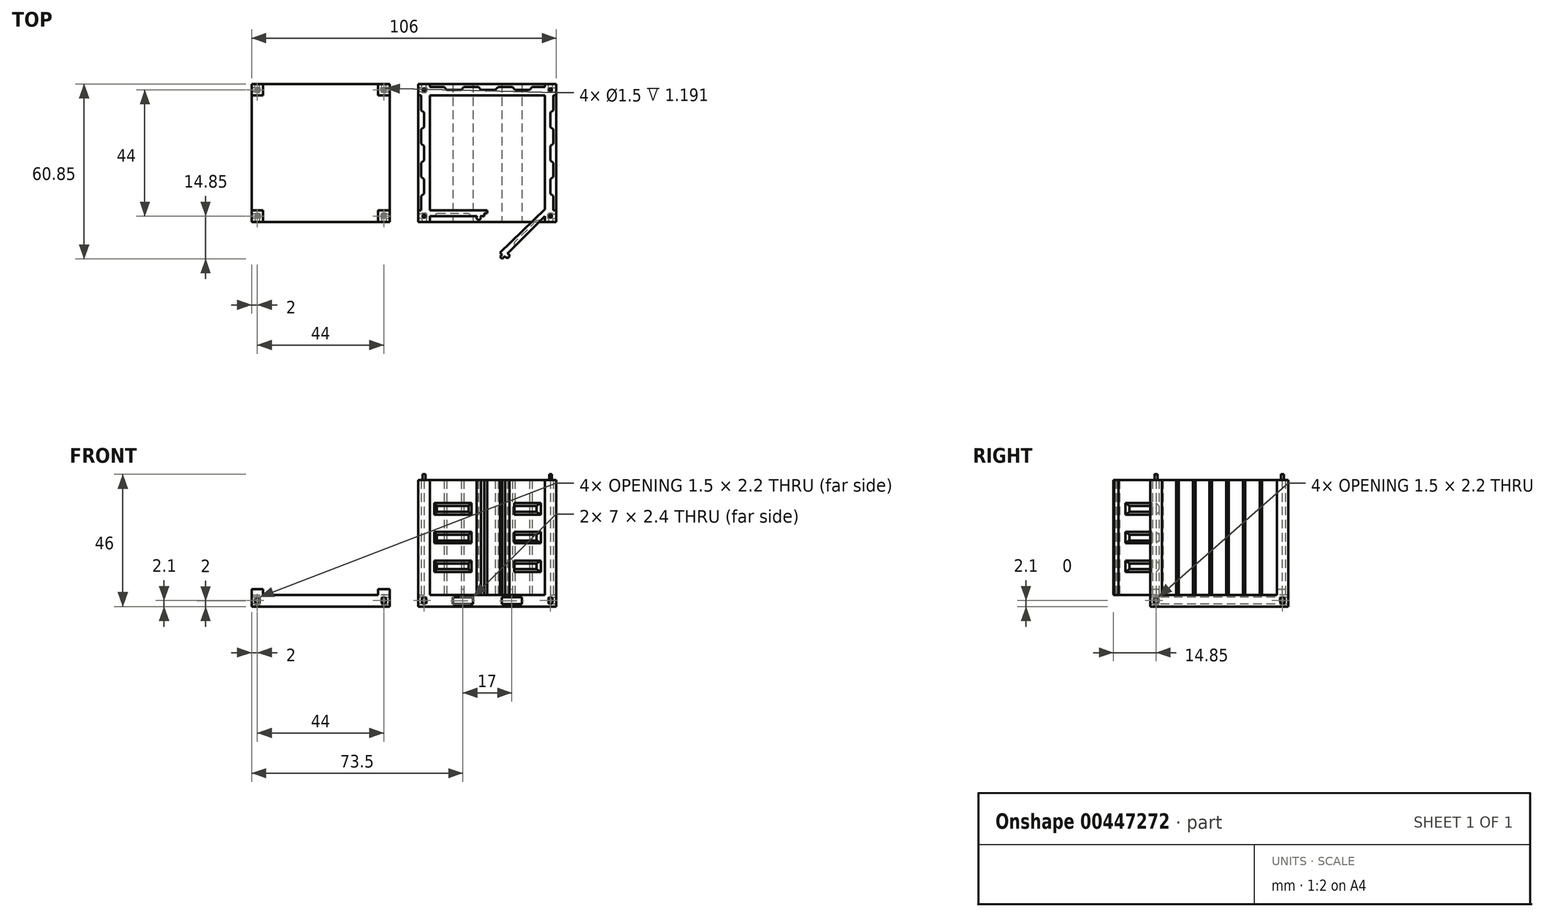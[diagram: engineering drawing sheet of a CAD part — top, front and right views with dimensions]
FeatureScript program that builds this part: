
annotation { "Feature Type Name" : "Feature", "Feature Type Description" : "" }
export const myFeature = defineFeature(function(context is Context, id is Id, definition is map)
    precondition{}
    {
        {
            var Q0;
            Q0=qCreatedBy(makeId("Top.planeOp"),FACE);
            var sketch = newSketch(context, id + "F0", { "sketchPlane" : qUnion([Q0])});
            skLineSegment(sketch, "E0.bottom", {"start": v(0, 0) * mm, "end": v(48, 0) * mm});
            skLineSegment(sketch, "E0.top", {"start": v(0, 48) * mm, "end": v(48, 48) * mm});
            skLineSegment(sketch, "E0.left", {"start": v(0, 0) * mm, "end": v(0, 48) * mm});
            skLineSegment(sketch, "E0.right", {"start": v(48, 0) * mm, "end": v(48, 48) * mm});
            skSolve(sketch);
        }
        {
            var Q0;
            Q0 = qSketchRegion(id + "F0", true);
            extrude(context, id + "F1", {"entities" : qUnion([Q0]), "depth" : 4 * mm});
        }
        {
            var Q0;
            Q0=makeQuery(id+"F1.opExtrude","SWEPT_FACE",FACE,{"disambiguationData":[OSD([sQuery(id+"F0.wireOp",EDGE,"E0.bottom")])]});
            var sketch = newSketch(context, id + "F2", { "sketchPlane" : qUnion([Q0])});
            skLineSegment(sketch, "E1", {"start": v(0, 2) * mm, "end": v(48, 2) * mm, "construction": true});
            skLineSegment(sketch, "E2", {"start": v(24, 2) * mm, "end": v(29, 2) * mm, "construction": true});
            skLineSegment(sketch, "E3", {"start": v(29, 2) * mm, "end": v(29, 3.2) * mm});
            skLineSegment(sketch, "E4", {"start": v(29, 3.2) * mm, "end": v(36, 3.2) * mm});
            skLineSegment(sketch, "E5", {"start": v(36, 3.2) * mm, "end": v(36, 0.8) * mm});
            skLineSegment(sketch, "E6", {"start": v(36, 0.8) * mm, "end": v(29, 0.8) * mm});
            skLineSegment(sketch, "E7", {"start": v(29, 0.8) * mm, "end": v(29, 2) * mm});
            skLineSegment(sketch, "E8", {"start": v(24, 2) * mm, "end": v(24, -4.17) * mm, "construction": true});
            skLineSegment(sketch, "E9.MirrorCS", {"start": v(19, 3.2) * mm, "end": v(12, 3.2) * mm});
            skLineSegment(sketch, "E10.MirrorCS", {"start": v(19, 2) * mm, "end": v(19, 3.2) * mm});
            skLineSegment(sketch, "E11.MirrorCS", {"start": v(19, 0.8) * mm, "end": v(19, 2) * mm});
            skLineSegment(sketch, "E12.MirrorCS", {"start": v(12, 0.8) * mm, "end": v(19, 0.8) * mm});
            skLineSegment(sketch, "E13.MirrorCS", {"start": v(12, 3.2) * mm, "end": v(12, 0.8) * mm});
            skSolve(sketch);
        }
        {
            var Q0;
            Q0 = qSketchRegion(id + "F2", true);
            extrude(context, id + "F3", {"entities" : qUnion([Q0]), "operationType" : NewBodyOperationType.REMOVE, "oppositeDirection" : true, "depth" : 48 * mm});
        }
        {
            var Q0;
            Q0=makeQuery(id+"F1.opExtrude","CAP_FACE",FACE,{"disambiguationData":[OSD([sQuery(id+"F0.wireOp",EDGE,"E0.bottom"),sQuery(id+"F0.wireOp",EDGE,"E0.top"),sQuery(id+"F0.wireOp",EDGE,"E0.left"),sQuery(id+"F0.wireOp",EDGE,"E0.right")])],"isStart":false});
            var sketch = newSketch(context, id + "F4", { "sketchPlane" : qUnion([Q0])});
            skLineSegment(sketch, "E14.bottom", {"start": v(0, 48) * mm, "end": v(4, 48) * mm});
            skLineSegment(sketch, "E14.top", {"start": v(0, 44) * mm, "end": v(1, 44) * mm});
            skLineSegment(sketch, "E14.left", {"start": v(0, 48) * mm, "end": v(0, 44) * mm});
            skLineSegment(sketch, "E14.right", {"start": v(4, 48) * mm, "end": v(4, 47) * mm});
            skLineSegment(sketch, "E15.bottom", {"start": v(48, 48) * mm, "end": v(44, 48) * mm});
            skLineSegment(sketch, "E15.top", {"start": v(48, 44) * mm, "end": v(47, 44) * mm});
            skLineSegment(sketch, "E15.left", {"start": v(48, 48) * mm, "end": v(48, 44) * mm});
            skLineSegment(sketch, "E15.right", {"start": v(44, 48) * mm, "end": v(44, 47) * mm});
            skLineSegment(sketch, "E16.bottom", {"start": v(48, 0) * mm, "end": v(44, 0) * mm});
            skLineSegment(sketch, "E16.top", {"start": v(48, 4) * mm, "end": v(47, 4) * mm});
            skLineSegment(sketch, "E16.left", {"start": v(48, 0) * mm, "end": v(48, 4) * mm});
            skLineSegment(sketch, "E16.right", {"start": v(44, 0) * mm, "end": v(44, 2) * mm});
            skLineSegment(sketch, "E17.bottom", {"start": v(0, 0) * mm, "end": v(4, 0) * mm});
            skLineSegment(sketch, "E17.top", {"start": v(0, 4) * mm, "end": v(1, 4) * mm});
            skLineSegment(sketch, "E17.left", {"start": v(0, 0) * mm, "end": v(0, 4) * mm});
            skLineSegment(sketch, "E17.right", {"start": v(4, 0) * mm, "end": v(4, 2) * mm});
            skLineSegment(sketch, "E18", {"start": v(1, 4) * mm, "end": v(0, 4) * mm, "construction": true});
            skLineSegment(sketch, "E19", {"start": v(1, 4) * mm, "end": v(1, 9) * mm});
            skLineSegment(sketch, "E20", {"start": v(1, 9) * mm, "end": v(2, 9.84) * mm});
            skLineSegment(sketch, "E21", {"start": v(2, 9.84) * mm, "end": v(2, 14.84) * mm});
            skLineSegment(sketch, "E22", {"start": v(2, 14.84) * mm, "end": v(1, 15.68) * mm});
            skLineSegment(sketch, "E23.0.1.0", {"start": v(1, 15.6) * mm, "end": v(1, 20.6) * mm});
            skLineSegment(sketch, "E23.0.1.1", {"start": v(1, 20.6) * mm, "end": v(2, 21.44) * mm});
            skLineSegment(sketch, "E23.0.1.2", {"start": v(2, 21.44) * mm, "end": v(2, 26.44) * mm});
            skLineSegment(sketch, "E23.0.1.3", {"start": v(2, 26.44) * mm, "end": v(1, 27.28) * mm});
            skLineSegment(sketch, "E23.0.2.0", {"start": v(1, 27.2) * mm, "end": v(1, 32.2) * mm});
            skLineSegment(sketch, "E23.0.2.1", {"start": v(1, 32.2) * mm, "end": v(2, 33.04) * mm});
            skLineSegment(sketch, "E23.0.2.2", {"start": v(2, 33.04) * mm, "end": v(2, 38.04) * mm});
            skLineSegment(sketch, "E23.0.2.3", {"start": v(2, 38.04) * mm, "end": v(1, 38.88) * mm});
            skLineSegment(sketch, "E23.direction1", {"start": v(1, 4) * mm, "end": v(1.1, 4.1) * mm, "construction": true});
            skLineSegment(sketch, "E23.direction2", {"start": v(1, 4) * mm, "end": v(1, 15.6) * mm, "construction": true});
            skLineSegment(sketch, "E24", {"start": v(1, 38.88) * mm, "end": v(1, 44) * mm});
            skLineSegment(sketch, "E25", {"start": v(24, 0) * mm, "end": v(24, -4.5) * mm, "construction": true});
            skLineSegment(sketch, "E26.MirrorCS", {"start": v(47, 9) * mm, "end": v(46, 9.84) * mm});
            skLineSegment(sketch, "E27.MirrorCS", {"start": v(46, 9.84) * mm, "end": v(46, 14.84) * mm});
            skLineSegment(sketch, "E28.MirrorCS", {"start": v(46, 14.84) * mm, "end": v(47, 15.68) * mm});
            skLineSegment(sketch, "E29.MirrorCS", {"start": v(47, 15.6) * mm, "end": v(47, 20.6) * mm});
            skLineSegment(sketch, "E30.MirrorCS", {"start": v(47, 20.6) * mm, "end": v(46, 21.44) * mm});
            skLineSegment(sketch, "E31.MirrorCS", {"start": v(46, 21.44) * mm, "end": v(46, 26.44) * mm});
            skLineSegment(sketch, "E32.MirrorCS", {"start": v(46, 26.44) * mm, "end": v(47, 27.28) * mm});
            skLineSegment(sketch, "E33.MirrorCS", {"start": v(47, 27.2) * mm, "end": v(47, 32.2) * mm});
            skLineSegment(sketch, "E34.MirrorCS", {"start": v(47, 32.2) * mm, "end": v(46, 33.04) * mm});
            skLineSegment(sketch, "E35.MirrorCS", {"start": v(46, 33.04) * mm, "end": v(46, 38.04) * mm});
            skLineSegment(sketch, "E36.MirrorCS", {"start": v(46, 38.04) * mm, "end": v(47, 38.88) * mm});
            skLineSegment(sketch, "E37.MirrorCS", {"start": v(47, 38.88) * mm, "end": v(47, 44) * mm});
            skLineSegment(sketch, "E38", {"start": v(47, 9) * mm, "end": v(47, 4) * mm});
            skLineSegment(sketch, "E39", {"start": v(4, 48) * mm, "end": v(4, 47) * mm, "construction": true});
            skLineSegment(sketch, "E40", {"start": v(4, 47) * mm, "end": v(9, 47) * mm});
            skLineSegment(sketch, "E41", {"start": v(9, 47) * mm, "end": v(9.93, 45.9) * mm});
            skLineSegment(sketch, "E42", {"start": v(9.93, 45.9) * mm, "end": v(14.93, 45.9) * mm});
            skLineSegment(sketch, "E43", {"start": v(14.93, 45.9) * mm, "end": v(15.86, 47) * mm});
            skLineSegment(sketch, "E44", {"start": v(15.86, 47) * mm, "end": v(20.86, 47) * mm});
            skLineSegment(sketch, "E45", {"start": v(20.86, 47) * mm, "end": v(21.79, 45.9) * mm});
            skLineSegment(sketch, "E46", {"start": v(21.79, 45.9) * mm, "end": v(26.79, 45.9) * mm});
            skLineSegment(sketch, "E47", {"start": v(26.79, 45.9) * mm, "end": v(27.71, 47) * mm});
            skLineSegment(sketch, "E48", {"start": v(27.71, 47) * mm, "end": v(32.71, 47) * mm});
            skLineSegment(sketch, "E49", {"start": v(32.71, 47) * mm, "end": v(33.64, 45.9) * mm});
            skLineSegment(sketch, "E50", {"start": v(33.64, 45.9) * mm, "end": v(38.64, 45.9) * mm});
            skLineSegment(sketch, "E51", {"start": v(38.64, 45.9) * mm, "end": v(39.57, 47) * mm});
            skLineSegment(sketch, "E52", {"start": v(39.57, 47) * mm, "end": v(44, 47) * mm});
            skLineSegment(sketch, "E53", {"start": v(4, 2) * mm, "end": v(20.44, 2) * mm});
            skLineSegment(sketch, "E54", {"start": v(23, 2) * mm, "end": v(23, 3) * mm});
            skLineSegment(sketch, "E55", {"start": v(23, 3) * mm, "end": v(24, 3) * mm});
            skLineSegment(sketch, "E56", {"start": v(24, 3) * mm, "end": v(24, 4) * mm});
            skLineSegment(sketch, "E57", {"start": v(24, 4) * mm, "end": v(4, 4) * mm});
            skLineSegment(sketch, "E58", {"start": v(44, 2) * mm, "end": v(30.96, -11.04) * mm});
            skLineSegment(sketch, "E59", {"start": v(29.15, -12.85) * mm, "end": v(28.44, -12.14) * mm});
            skLineSegment(sketch, "E60", {"start": v(28.44, -12.14) * mm, "end": v(29.15, -11.44) * mm});
            skLineSegment(sketch, "E61", {"start": v(29.15, -11.44) * mm, "end": v(28.44, -10.73) * mm});
            skLineSegment(sketch, "E62", {"start": v(28.44, -10.73) * mm, "end": v(44, 4.37) * mm});
            skLineSegment(sketch, "E63", {"start": v(44, 4.37) * mm, "end": v(44, 44) * mm});
            skLineSegment(sketch, "E64", {"start": v(44, 44) * mm, "end": v(4, 44) * mm});
            skLineSegment(sketch, "E65", {"start": v(4, 44) * mm, "end": v(4, 4) * mm});
            skPoint(sketch, "E66.orphan", {"position": v(4, 46) * mm});
            skPoint(sketch, "E67.orphan", {"position": v(44, 4) * mm});
            skPoint(sketch, "E68.orphan", {"position": v(2, 4) * mm});
            skLineSegment(sketch, "E69", {"start": v(23, 2) * mm, "end": v(21.56, 2) * mm, "construction": true});
            skLineSegment(sketch, "E70", {"start": v(21, 2) * mm, "end": v(21, 1.5) * mm, "construction": true});
            skArc(sketch, "E71", {"start": v(20.44, 2) * mm, "mid": v(21, 0.75) * mm, "end": v(21.56, 2) * mm});
            skLineSegment(sketch, "E72.trimOffspring", {"start": v(21.56, 2) * mm, "end": v(23, 2) * mm});
            skLineSegment(sketch, "E73", {"start": v(29.15, -12.85) * mm, "end": v(30.17, -11.83) * mm, "construction": true});
            skLineSegment(sketch, "E74", {"start": v(30.56, -11.44) * mm, "end": v(30.92, -11.79) * mm, "construction": true});
            skArc(sketch, "E75", {"start": v(30.17, -11.83) * mm, "mid": v(31.45, -12.32) * mm, "end": v(30.96, -11.04) * mm});
            skLineSegment(sketch, "E76.trimOffspring", {"start": v(30.17, -11.83) * mm, "end": v(29.15, -12.85) * mm});
            skSolve(sketch);
        }
        {
            var Q0;
            Q0 = qSketchRegion(id + "F4", true);
            extrude(context, id + "F5", {"entities" : qUnion([Q0]), "operationType" : NewBodyOperationType.ADD, "depth" : 40 * mm});
        }
        {
            var Q0;
            Q0=makeQuery(id+"F5.opExtrude","SWEPT_FACE",FACE,{"disambiguationData":[OSD([sQuery(id+"F4.wireOp",EDGE,"E53")])]});
            var sketch = newSketch(context, id + "F6", { "sketchPlane" : qUnion([Q0])});
            skLineSegment(sketch, "E77", {"start": v(4, 24) * mm, "end": v(5.5, 24) * mm, "construction": true});
            skLineSegment(sketch, "E78", {"start": v(5.5, 24) * mm, "end": v(5.5, 26) * mm});
            skLineSegment(sketch, "E79", {"start": v(5.5, 26) * mm, "end": v(18.5, 26) * mm});
            skLineSegment(sketch, "E80", {"start": v(18.5, 26) * mm, "end": v(18.5, 22) * mm});
            skLineSegment(sketch, "E81", {"start": v(18.5, 22) * mm, "end": v(5.5, 22) * mm});
            skLineSegment(sketch, "E82", {"start": v(5.5, 22) * mm, "end": v(5.5, 24) * mm});
            skLineSegment(sketch, "E83", {"start": v(4, 24) * mm, "end": v(4, 4) * mm, "construction": true});
            skPoint(sketch, "E84", {"position": v(4, 14) * mm});
            skLineSegment(sketch, "E85", {"start": v(4, 24) * mm, "end": v(4, 19) * mm, "construction": true});
            skLineSegment(sketch, "E86", {"start": v(4, 19) * mm, "end": v(-6.02, 19) * mm, "construction": true});
            skLineSegment(sketch, "E87.MirrorCS", {"start": v(5.5, 12) * mm, "end": v(18.5, 12) * mm});
            skLineSegment(sketch, "E88.MirrorCS", {"start": v(5.5, 14) * mm, "end": v(5.5, 12) * mm});
            skLineSegment(sketch, "E89.MirrorCS", {"start": v(5.5, 16) * mm, "end": v(5.5, 14) * mm});
            skLineSegment(sketch, "E90.MirrorCS", {"start": v(18.5, 16) * mm, "end": v(5.5, 16) * mm});
            skLineSegment(sketch, "E91.MirrorCS", {"start": v(18.5, 12) * mm, "end": v(18.5, 16) * mm});
            skLineSegment(sketch, "E92", {"start": v(4, 24) * mm, "end": v(4, 29) * mm, "construction": true});
            skLineSegment(sketch, "E93", {"start": v(4, 29) * mm, "end": v(-8.26, 29) * mm, "construction": true});
            skLineSegment(sketch, "E94.MirrorCS", {"start": v(5.5, 32) * mm, "end": v(18.5, 32) * mm});
            skLineSegment(sketch, "E95.MirrorCS", {"start": v(5.5, 34) * mm, "end": v(5.5, 32) * mm});
            skLineSegment(sketch, "E96.MirrorCS", {"start": v(5.5, 36) * mm, "end": v(5.5, 34) * mm});
            skLineSegment(sketch, "E97.MirrorCS", {"start": v(18.5, 36) * mm, "end": v(5.5, 36) * mm});
            skLineSegment(sketch, "E98.MirrorCS", {"start": v(18.5, 32) * mm, "end": v(18.5, 36) * mm});
            skSolve(sketch);
        }
        {
            var Q0;
            Q0 = qSketchRegion(id + "F6", true);
            extrude(context, id + "F7", {"entities" : qUnion([Q0]), "operationType" : NewBodyOperationType.REMOVE, "oppositeDirection" : true, "depth" : 1 * mm, "hasDraft" : true, "draftAngle" : 45 * degree, "draftPullDirection" : true});
        }
        {
            var Q0;
            Q0=makeQuery(id+"F5.opExtrude","SWEPT_FACE",FACE,{"disambiguationData":[OSD([sQuery(id+"F4.wireOp",EDGE,"E58")])]});
            var sketch = newSketch(context, id + "F8", { "sketchPlane" : qUnion([Q0])});
            skLineSegment(sketch, "E99", {"start": v(32.53, 24) * mm, "end": v(30.53, 24) * mm, "construction": true});
            skLineSegment(sketch, "E100", {"start": v(30.53, 24) * mm, "end": v(30.53, 22) * mm});
            skLineSegment(sketch, "E101", {"start": v(30.53, 22) * mm, "end": v(17.53, 22) * mm});
            skLineSegment(sketch, "E102", {"start": v(17.53, 22) * mm, "end": v(17.53, 26) * mm});
            skLineSegment(sketch, "E103", {"start": v(17.53, 26) * mm, "end": v(30.53, 26) * mm});
            skLineSegment(sketch, "E104", {"start": v(30.53, 26) * mm, "end": v(30.53, 24) * mm});
            skLineSegment(sketch, "E105", {"start": v(30.53, 24) * mm, "end": v(30.53, 29) * mm, "construction": true});
            skLineSegment(sketch, "E106", {"start": v(30.53, 29) * mm, "end": v(36.07, 29) * mm, "construction": true});
            skLineSegment(sketch, "E107.MirrorCS", {"start": v(17.53, 32) * mm, "end": v(30.53, 32) * mm});
            skLineSegment(sketch, "E108.MirrorCS", {"start": v(17.53, 36) * mm, "end": v(17.53, 32) * mm});
            skLineSegment(sketch, "E109.MirrorCS", {"start": v(30.53, 36) * mm, "end": v(17.53, 36) * mm});
            skLineSegment(sketch, "E110.MirrorCS", {"start": v(30.53, 34) * mm, "end": v(30.53, 36) * mm});
            skLineSegment(sketch, "E111.MirrorCS", {"start": v(30.53, 34) * mm, "end": v(30.53, 29) * mm, "construction": true});
            skLineSegment(sketch, "E112", {"start": v(30.53, 34) * mm, "end": v(30.53, 32) * mm});
            skLineSegment(sketch, "E113", {"start": v(30.53, 24) * mm, "end": v(30.53, 19) * mm, "construction": true});
            skLineSegment(sketch, "E114", {"start": v(30.53, 19) * mm, "end": v(38.33, 19) * mm, "construction": true});
            skLineSegment(sketch, "E115.MirrorCS", {"start": v(30.53, 16) * mm, "end": v(17.53, 16) * mm});
            skLineSegment(sketch, "E116.MirrorCS", {"start": v(17.53, 16) * mm, "end": v(17.53, 12) * mm});
            skLineSegment(sketch, "E117.MirrorCS", {"start": v(17.53, 12) * mm, "end": v(30.53, 12) * mm});
            skLineSegment(sketch, "E118", {"start": v(30.53, 16) * mm, "end": v(30.53, 12) * mm});
            skSolve(sketch);
        }
        {
            var Q0;
            Q0 = qSketchRegion(id + "F8", true);
            extrude(context, id + "F9", {"entities" : qUnion([Q0]), "operationType" : NewBodyOperationType.REMOVE, "oppositeDirection" : true, "depth" : 1 * mm, "hasDraft" : true, "draftAngle" : 45 * degree, "draftPullDirection" : true});
        }
        {
            var Q0;
            Q0=makeQuery(id+"F5.opExtrude","CAP_FACE",FACE,{"disambiguationData":[OSD([sQuery(id+"F4.wireOp",EDGE,"E14.bottom"),sQuery(id+"F4.wireOp",EDGE,"E14.top"),sQuery(id+"F4.wireOp",EDGE,"E14.left"),sQuery(id+"F4.wireOp",EDGE,"E14.right"),sQuery(id+"F4.wireOp",EDGE,"E15.bottom"),sQuery(id+"F4.wireOp",EDGE,"E15.top"),sQuery(id+"F4.wireOp",EDGE,"E15.left"),sQuery(id+"F4.wireOp",EDGE,"E15.right"),sQuery(id+"F4.wireOp",EDGE,"E16.bottom"),sQuery(id+"F4.wireOp",EDGE,"E16.top"),sQuery(id+"F4.wireOp",EDGE,"E16.left"),sQuery(id+"F4.wireOp",EDGE,"E16.right"),sQuery(id+"F4.wireOp",EDGE,"E17.bottom"),sQuery(id+"F4.wireOp",EDGE,"E17.top"),sQuery(id+"F4.wireOp",EDGE,"E17.left"),sQuery(id+"F4.wireOp",EDGE,"E17.right"),sQuery(id+"F4.wireOp",EDGE,"E19"),sQuery(id+"F4.wireOp",EDGE,"E20"),sQuery(id+"F4.wireOp",EDGE,"E21"),sQuery(id+"F4.wireOp",EDGE,"E22"),sQuery(id+"F4.wireOp",EDGE,"E23.0.1.0"),sQuery(id+"F4.wireOp",EDGE,"E23.0.1.1"),sQuery(id+"F4.wireOp",EDGE,"E23.0.1.2"),sQuery(id+"F4.wireOp",EDGE,"E23.0.1.3"),sQuery(id+"F4.wireOp",EDGE,"E23.0.2.0"),sQuery(id+"F4.wireOp",EDGE,"E23.0.2.1"),sQuery(id+"F4.wireOp",EDGE,"E23.0.2.2"),sQuery(id+"F4.wireOp",EDGE,"E23.0.2.3"),sQuery(id+"F4.wireOp",EDGE,"E24"),sQuery(id+"F4.wireOp",EDGE,"E26.MirrorCS"),sQuery(id+"F4.wireOp",EDGE,"E27.MirrorCS"),sQuery(id+"F4.wireOp",EDGE,"E28.MirrorCS"),sQuery(id+"F4.wireOp",EDGE,"E29.MirrorCS"),sQuery(id+"F4.wireOp",EDGE,"E30.MirrorCS"),sQuery(id+"F4.wireOp",EDGE,"E31.MirrorCS"),sQuery(id+"F4.wireOp",EDGE,"E32.MirrorCS"),sQuery(id+"F4.wireOp",EDGE,"E33.MirrorCS"),sQuery(id+"F4.wireOp",EDGE,"E34.MirrorCS"),sQuery(id+"F4.wireOp",EDGE,"E35.MirrorCS"),sQuery(id+"F4.wireOp",EDGE,"E36.MirrorCS"),sQuery(id+"F4.wireOp",EDGE,"E37.MirrorCS"),sQuery(id+"F4.wireOp",EDGE,"E38"),sQuery(id+"F4.wireOp",EDGE,"E40"),sQuery(id+"F4.wireOp",EDGE,"E41"),sQuery(id+"F4.wireOp",EDGE,"E42"),sQuery(id+"F4.wireOp",EDGE,"E43"),sQuery(id+"F4.wireOp",EDGE,"E44"),sQuery(id+"F4.wireOp",EDGE,"E45"),sQuery(id+"F4.wireOp",EDGE,"E46"),sQuery(id+"F4.wireOp",EDGE,"E47"),sQuery(id+"F4.wireOp",EDGE,"E48"),sQuery(id+"F4.wireOp",EDGE,"E49"),sQuery(id+"F4.wireOp",EDGE,"E50"),sQuery(id+"F4.wireOp",EDGE,"E51"),sQuery(id+"F4.wireOp",EDGE,"E52"),sQuery(id+"F4.wireOp",EDGE,"E53"),sQuery(id+"F4.wireOp",EDGE,"E54"),sQuery(id+"F4.wireOp",EDGE,"E55"),sQuery(id+"F4.wireOp",EDGE,"E56"),sQuery(id+"F4.wireOp",EDGE,"E57"),sQuery(id+"F4.wireOp",EDGE,"E58"),sQuery(id+"F4.wireOp",EDGE,"E59"),sQuery(id+"F4.wireOp",EDGE,"E60"),sQuery(id+"F4.wireOp",EDGE,"E61"),sQuery(id+"F4.wireOp",EDGE,"E62"),sQuery(id+"F4.wireOp",EDGE,"E63"),sQuery(id+"F4.wireOp",EDGE,"E64"),sQuery(id+"F4.wireOp",EDGE,"E65"),sQuery(id+"F4.wireOp",EDGE,"E71"),sQuery(id+"F4.wireOp",EDGE,"E72.trimOffspring"),sQuery(id+"F4.wireOp",EDGE,"E75"),sQuery(id+"F4.wireOp",EDGE,"E76.trimOffspring")])],"isStart":false});
            var sketch = newSketch(context, id + "F10", { "sketchPlane" : qUnion([Q0])});
            skCircle(sketch, "E119", {"center": v(2, 46) * mm, "radius": 0.5 * mm});
            skPoint(sketch, "E119.centerSnap0", {"position": v(2, 48) * mm});
            skPoint(sketch, "E119.centerSnap1", {"position": v(0, 46) * mm});
            skCircle(sketch, "E120", {"center": v(46, 46) * mm, "radius": 0.5 * mm});
            skPoint(sketch, "E120.centerSnap0", {"position": v(48, 46) * mm});
            skPoint(sketch, "E120.centerSnap1", {"position": v(46, 48) * mm});
            skCircle(sketch, "E121", {"center": v(46, 2) * mm, "radius": 0.5 * mm});
            skPoint(sketch, "E121.centerSnap0", {"position": v(48, 2) * mm});
            skPoint(sketch, "E121.centerSnap1", {"position": v(46, 0) * mm});
            skCircle(sketch, "E122", {"center": v(2, 2) * mm, "radius": 0.5 * mm});
            skPoint(sketch, "E122.centerSnap0", {"position": v(0, 2) * mm});
            skPoint(sketch, "E122.centerSnap1", {"position": v(2, 0) * mm});
            skSolve(sketch);
        }
        {
            var Q0;
            Q0 = qSketchRegion(id + "F10", true);
            extrude(context, id + "F11", {"entities" : qUnion([Q0]), "operationType" : NewBodyOperationType.ADD, "depth" : 2 * mm});
        }
        {
            var Q0;
            Q0=makeQuery(id+"F5.boolean.opBoolean","MERGE",FACE,{"derivedFrom":[makeQuery(id+"F1.opExtrude","SWEPT_FACE",FACE,{"disambiguationData":[OSD([sQuery(id+"F0.wireOp",EDGE,"E0.right")])]}),makeQuery(id+"F5.opExtrude","SWEPT_FACE",FACE,{"disambiguationData":[OSD([sQuery(id+"F4.wireOp",EDGE,"E15.left")])]}),makeQuery(id+"F5.opExtrude","SWEPT_FACE",FACE,{"disambiguationData":[OSD([sQuery(id+"F4.wireOp",EDGE,"E16.left")])]})]});
            var sketch = newSketch(context, id + "F12", { "sketchPlane" : qUnion([Q0])});
            skLineSegment(sketch, "E123", {"start": v(48, 0) * mm, "end": v(46, 0) * mm, "construction": true});
            skLineSegment(sketch, "E124", {"start": v(46, 0) * mm, "end": v(46, 1) * mm, "construction": true});
            skLineSegment(sketch, "E125", {"start": v(46, 1) * mm, "end": v(46.05, 1) * mm});
            skLineSegment(sketch, "E126", {"start": v(46.75, 1.7) * mm, "end": v(46.75, 2.5) * mm});
            skLineSegment(sketch, "E127", {"start": v(46.05, 3.2) * mm, "end": v(45.95, 3.2) * mm});
            skLineSegment(sketch, "E128", {"start": v(45.25, 2.5) * mm, "end": v(45.25, 1.7) * mm});
            skLineSegment(sketch, "E129", {"start": v(45.95, 1) * mm, "end": v(46, 1) * mm});
            skPoint(sketch, "E130.visualSharp", {"position": v(46.75, 3.2) * mm});
            skArc(sketch, "E130.filletArc", {"start": v(46.75, 2.5) * mm, "mid": v(46.54, 3) * mm, "end": v(46.05, 3.2) * mm});
            skPoint(sketch, "E131.visualSharp", {"position": v(45.25, 3.2) * mm});
            skArc(sketch, "E131.filletArc", {"start": v(45.95, 3.2) * mm, "mid": v(45.46, 3) * mm, "end": v(45.25, 2.5) * mm});
            skPoint(sketch, "E132.visualSharp", {"position": v(45.25, 1) * mm});
            skArc(sketch, "E132.filletArc", {"start": v(45.25, 1.7) * mm, "mid": v(45.46, 1.2) * mm, "end": v(45.95, 1) * mm});
            skPoint(sketch, "E133.visualSharp", {"position": v(46.75, 1) * mm});
            skArc(sketch, "E133.filletArc", {"start": v(46.05, 1) * mm, "mid": v(46.54, 1.2) * mm, "end": v(46.75, 1.7) * mm});
            skLineSegment(sketch, "E134", {"start": v(24, 0) * mm, "end": v(24, -3.6) * mm, "construction": true});
            skArc(sketch, "E135.MirrorCS", {"start": v(2.05, 3.2) * mm, "mid": v(2.54, 3) * mm, "end": v(2.75, 2.5) * mm});
            skLineSegment(sketch, "E136.MirrorCS", {"start": v(2.75, 2.5) * mm, "end": v(2.75, 1.7) * mm});
            skArc(sketch, "E137.MirrorCS", {"start": v(2.75, 1.7) * mm, "mid": v(2.54, 1.2) * mm, "end": v(2.05, 1) * mm});
            skLineSegment(sketch, "E138.MirrorCS", {"start": v(2.05, 1) * mm, "end": v(2, 1) * mm});
            skLineSegment(sketch, "E139.MirrorCS", {"start": v(2, 1) * mm, "end": v(1.95, 1) * mm});
            skArc(sketch, "E140.MirrorCS", {"start": v(1.95, 1) * mm, "mid": v(1.46, 1.2) * mm, "end": v(1.25, 1.7) * mm});
            skLineSegment(sketch, "E141.MirrorCS", {"start": v(1.25, 1.7) * mm, "end": v(1.25, 2.5) * mm});
            skArc(sketch, "E142.MirrorCS", {"start": v(1.25, 2.5) * mm, "mid": v(1.46, 3) * mm, "end": v(1.95, 3.2) * mm});
            skLineSegment(sketch, "E143.MirrorCS", {"start": v(1.95, 3.2) * mm, "end": v(2.05, 3.2) * mm});
            skSolve(sketch);
        }
        {
            var Q0;
            Q0 = qSketchRegion(id + "F12", true);
            extrude(context, id + "F13", {"entities" : qUnion([Q0]), "operationType" : NewBodyOperationType.REMOVE, "oppositeDirection" : true, "depth" : 3 * mm});
        }
        {
            var Q0;
            Q0=makeQuery(id+"F5.boolean.opBoolean","MERGE",FACE,{"derivedFrom":[makeQuery(id+"F1.opExtrude","SWEPT_FACE",FACE,{"disambiguationData":[OSD([sQuery(id+"F0.wireOp",EDGE,"E0.top")])]}),makeQuery(id+"F5.opExtrude","SWEPT_FACE",FACE,{"disambiguationData":[OSD([sQuery(id+"F4.wireOp",EDGE,"E14.bottom")])]}),makeQuery(id+"F5.opExtrude","SWEPT_FACE",FACE,{"disambiguationData":[OSD([sQuery(id+"F4.wireOp",EDGE,"E15.bottom")])]})]});
            var sketch = newSketch(context, id + "F14", { "sketchPlane" : qUnion([Q0])});
            skLineSegment(sketch, "E144", {"start": v(-48, 0) * mm, "end": v(-46, 0) * mm, "construction": true});
            skLineSegment(sketch, "E145", {"start": v(-46, 0) * mm, "end": v(-46, 1) * mm, "construction": true});
            skLineSegment(sketch, "E146", {"start": v(-46, 1) * mm, "end": v(-45.95, 1) * mm});
            skLineSegment(sketch, "E147", {"start": v(-45.25, 1.7) * mm, "end": v(-45.25, 2.5) * mm});
            skLineSegment(sketch, "E148", {"start": v(-45.95, 3.2) * mm, "end": v(-46.05, 3.2) * mm});
            skLineSegment(sketch, "E149", {"start": v(-46.75, 2.5) * mm, "end": v(-46.75, 1.7) * mm});
            skLineSegment(sketch, "E150", {"start": v(-46.05, 1) * mm, "end": v(-46, 1) * mm});
            skPoint(sketch, "E151.visualSharp", {"position": v(-45.25, 3.2) * mm});
            skArc(sketch, "E151.filletArc", {"start": v(-45.25, 2.5) * mm, "mid": v(-45.46, 3) * mm, "end": v(-45.95, 3.2) * mm});
            skPoint(sketch, "E152.visualSharp", {"position": v(-46.75, 3.2) * mm});
            skArc(sketch, "E152.filletArc", {"start": v(-46.05, 3.2) * mm, "mid": v(-46.54, 3) * mm, "end": v(-46.75, 2.5) * mm});
            skPoint(sketch, "E153.visualSharp", {"position": v(-45.25, 1) * mm});
            skArc(sketch, "E153.filletArc", {"start": v(-45.95, 1) * mm, "mid": v(-45.46, 1.2) * mm, "end": v(-45.25, 1.7) * mm});
            skPoint(sketch, "E154.visualSharp", {"position": v(-46.75, 1) * mm});
            skArc(sketch, "E154.filletArc", {"start": v(-46.75, 1.7) * mm, "mid": v(-46.54, 1.2) * mm, "end": v(-46.05, 1) * mm});
            skLineSegment(sketch, "E155", {"start": v(-24, 0) * mm, "end": v(-24, -2.27) * mm, "construction": true});
            skLineSegment(sketch, "E156.MirrorCS", {"start": v(-2.05, 3.2) * mm, "end": v(-1.95, 3.2) * mm});
            skArc(sketch, "E157.MirrorCS", {"start": v(-1.95, 3.2) * mm, "mid": v(-1.46, 3) * mm, "end": v(-1.25, 2.5) * mm});
            skLineSegment(sketch, "E158.MirrorCS", {"start": v(-1.25, 2.5) * mm, "end": v(-1.25, 1.7) * mm});
            skArc(sketch, "E159.MirrorCS", {"start": v(-1.25, 1.7) * mm, "mid": v(-1.46, 1.2) * mm, "end": v(-1.95, 1) * mm});
            skLineSegment(sketch, "E160.MirrorCS", {"start": v(-2, 1) * mm, "end": v(-2.05, 1) * mm});
            skLineSegment(sketch, "E161.MirrorCS", {"start": v(-1.95, 1) * mm, "end": v(-2, 1) * mm});
            skArc(sketch, "E162.MirrorCS", {"start": v(-2.05, 1) * mm, "mid": v(-2.54, 1.2) * mm, "end": v(-2.75, 1.7) * mm});
            skLineSegment(sketch, "E163.MirrorCS", {"start": v(-2.75, 1.7) * mm, "end": v(-2.75, 2.5) * mm});
            skArc(sketch, "E164.MirrorCS", {"start": v(-2.75, 2.5) * mm, "mid": v(-2.54, 3) * mm, "end": v(-2.05, 3.2) * mm});
            skSolve(sketch);
        }
        {
            var Q0;
            Q0 = qSketchRegion(id + "F14", true);
            extrude(context, id + "F15", {"entities" : qUnion([Q0]), "operationType" : NewBodyOperationType.REMOVE, "oppositeDirection" : true, "depth" : 3 * mm});
        }
        {
            var Q0;
            Q0=makeQuery(id+"F5.boolean.opBoolean","MERGE",FACE,{"derivedFrom":[makeQuery(id+"F1.opExtrude","SWEPT_FACE",FACE,{"disambiguationData":[OSD([sQuery(id+"F0.wireOp",EDGE,"E0.left")])]}),makeQuery(id+"F5.opExtrude","SWEPT_FACE",FACE,{"disambiguationData":[OSD([sQuery(id+"F4.wireOp",EDGE,"E14.left")])]}),makeQuery(id+"F5.opExtrude","SWEPT_FACE",FACE,{"disambiguationData":[OSD([sQuery(id+"F4.wireOp",EDGE,"E17.left")])]})]});
            var sketch = newSketch(context, id + "F16", { "sketchPlane" : qUnion([Q0])});
            skLineSegment(sketch, "E165", {"start": v(-48, 0) * mm, "end": v(-46, 0) * mm, "construction": true});
            skLineSegment(sketch, "E166", {"start": v(-46, 0) * mm, "end": v(-46, 1) * mm, "construction": true});
            skLineSegment(sketch, "E167", {"start": v(-46, 1) * mm, "end": v(-45.95, 1) * mm});
            skLineSegment(sketch, "E168", {"start": v(-45.25, 1.7) * mm, "end": v(-45.25, 2.5) * mm});
            skLineSegment(sketch, "E169", {"start": v(-45.95, 3.2) * mm, "end": v(-46.05, 3.2) * mm});
            skLineSegment(sketch, "E170", {"start": v(-46.75, 2.5) * mm, "end": v(-46.75, 1.7) * mm});
            skLineSegment(sketch, "E171", {"start": v(-46.05, 1) * mm, "end": v(-46, 1) * mm});
            skPoint(sketch, "E172.visualSharp", {"position": v(-45.25, 3.2) * mm});
            skArc(sketch, "E172.filletArc", {"start": v(-45.25, 2.5) * mm, "mid": v(-45.46, 3) * mm, "end": v(-45.95, 3.2) * mm});
            skPoint(sketch, "E173.visualSharp", {"position": v(-46.75, 3.2) * mm});
            skArc(sketch, "E173.filletArc", {"start": v(-46.05, 3.2) * mm, "mid": v(-46.54, 3) * mm, "end": v(-46.75, 2.5) * mm});
            skPoint(sketch, "E174.visualSharp", {"position": v(-46.75, 1) * mm});
            skArc(sketch, "E174.filletArc", {"start": v(-46.75, 1.7) * mm, "mid": v(-46.54, 1.2) * mm, "end": v(-46.05, 1) * mm});
            skPoint(sketch, "E175.visualSharp", {"position": v(-45.25, 1) * mm});
            skArc(sketch, "E175.filletArc", {"start": v(-45.95, 1) * mm, "mid": v(-45.46, 1.2) * mm, "end": v(-45.25, 1.7) * mm});
            skLineSegment(sketch, "E176", {"start": v(-24, 0) * mm, "end": v(-24, -2.88) * mm, "construction": true});
            skArc(sketch, "E177.MirrorCS", {"start": v(-1.95, 3.2) * mm, "mid": v(-1.46, 3) * mm, "end": v(-1.25, 2.5) * mm});
            skLineSegment(sketch, "E178.MirrorCS", {"start": v(-1.25, 2.5) * mm, "end": v(-1.25, 1.7) * mm});
            skArc(sketch, "E179.MirrorCS", {"start": v(-1.25, 1.7) * mm, "mid": v(-1.46, 1.2) * mm, "end": v(-1.95, 1) * mm});
            skLineSegment(sketch, "E180.MirrorCS", {"start": v(-1.95, 1) * mm, "end": v(-2, 1) * mm});
            skLineSegment(sketch, "E181.MirrorCS", {"start": v(-2, 1) * mm, "end": v(-2.05, 1) * mm});
            skArc(sketch, "E182.MirrorCS", {"start": v(-2.05, 1) * mm, "mid": v(-2.54, 1.2) * mm, "end": v(-2.75, 1.7) * mm});
            skLineSegment(sketch, "E183.MirrorCS", {"start": v(-2.75, 1.7) * mm, "end": v(-2.75, 2.5) * mm});
            skArc(sketch, "E184.MirrorCS", {"start": v(-2.75, 2.5) * mm, "mid": v(-2.54, 3) * mm, "end": v(-2.05, 3.2) * mm});
            skLineSegment(sketch, "E185.MirrorCS", {"start": v(-2.05, 3.2) * mm, "end": v(-1.95, 3.2) * mm});
            skSolve(sketch);
        }
        {
            var Q0;
            Q0 = qSketchRegion(id + "F16", true);
            extrude(context, id + "F17", {"entities" : qUnion([Q0]), "operationType" : NewBodyOperationType.REMOVE, "oppositeDirection" : true, "depth" : 3 * mm});
        }
        {
            var Q0;
            Q0=makeQuery(id+"F5.boolean.opBoolean","MERGE",FACE,{"derivedFrom":[makeQuery(id+"F1.opExtrude","SWEPT_FACE",FACE,{"disambiguationData":[OSD([sQuery(id+"F0.wireOp",EDGE,"E0.bottom")])]}),makeQuery(id+"F5.opExtrude","SWEPT_FACE",FACE,{"disambiguationData":[OSD([sQuery(id+"F4.wireOp",EDGE,"E16.bottom")])]}),makeQuery(id+"F5.opExtrude","SWEPT_FACE",FACE,{"disambiguationData":[OSD([sQuery(id+"F4.wireOp",EDGE,"E17.bottom")])]})]});
            var sketch = newSketch(context, id + "F18", { "sketchPlane" : qUnion([Q0])});
            skLineSegment(sketch, "E186", {"start": v(0, 0) * mm, "end": v(2, 0) * mm, "construction": true});
            skLineSegment(sketch, "E187", {"start": v(2, 0) * mm, "end": v(2, 1) * mm, "construction": true});
            skLineSegment(sketch, "E188", {"start": v(2, 1) * mm, "end": v(2.05, 1) * mm});
            skLineSegment(sketch, "E189", {"start": v(2.75, 1.7) * mm, "end": v(2.75, 2.5) * mm});
            skLineSegment(sketch, "E190", {"start": v(2.05, 3.2) * mm, "end": v(1.95, 3.2) * mm});
            skLineSegment(sketch, "E191", {"start": v(1.25, 2.5) * mm, "end": v(1.25, 1.7) * mm});
            skLineSegment(sketch, "E192", {"start": v(1.95, 1) * mm, "end": v(2, 1) * mm});
            skPoint(sketch, "E193.visualSharp", {"position": v(2.75, 3.2) * mm});
            skArc(sketch, "E193.filletArc", {"start": v(2.75, 2.5) * mm, "mid": v(2.54, 3) * mm, "end": v(2.05, 3.2) * mm});
            skPoint(sketch, "E194.visualSharp", {"position": v(2.75, 1) * mm});
            skArc(sketch, "E194.filletArc", {"start": v(2.05, 1) * mm, "mid": v(2.54, 1.2) * mm, "end": v(2.75, 1.7) * mm});
            skPoint(sketch, "E195.visualSharp", {"position": v(1.25, 1) * mm});
            skArc(sketch, "E195.filletArc", {"start": v(1.25, 1.7) * mm, "mid": v(1.46, 1.2) * mm, "end": v(1.95, 1) * mm});
            skPoint(sketch, "E196.visualSharp", {"position": v(1.25, 3.2) * mm});
            skArc(sketch, "E196.filletArc", {"start": v(1.95, 3.2) * mm, "mid": v(1.46, 3) * mm, "end": v(1.25, 2.5) * mm});
            skLineSegment(sketch, "E197", {"start": v(24, 0) * mm, "end": v(24, -4.75) * mm, "construction": true});
            skArc(sketch, "E198.MirrorCS", {"start": v(46.05, 3.2) * mm, "mid": v(46.54, 3) * mm, "end": v(46.75, 2.5) * mm});
            skLineSegment(sketch, "E199.MirrorCS", {"start": v(46.75, 2.5) * mm, "end": v(46.75, 1.7) * mm});
            skArc(sketch, "E200.MirrorCS", {"start": v(46.75, 1.7) * mm, "mid": v(46.54, 1.2) * mm, "end": v(46.05, 1) * mm});
            skLineSegment(sketch, "E201.MirrorCS", {"start": v(46.05, 1) * mm, "end": v(46, 1) * mm});
            skLineSegment(sketch, "E202.MirrorCS", {"start": v(46, 1) * mm, "end": v(45.95, 1) * mm});
            skArc(sketch, "E203.MirrorCS", {"start": v(45.95, 1) * mm, "mid": v(45.46, 1.2) * mm, "end": v(45.25, 1.7) * mm});
            skLineSegment(sketch, "E204.MirrorCS", {"start": v(45.25, 1.7) * mm, "end": v(45.25, 2.5) * mm});
            skArc(sketch, "E205.MirrorCS", {"start": v(45.25, 2.5) * mm, "mid": v(45.46, 3) * mm, "end": v(45.95, 3.2) * mm});
            skLineSegment(sketch, "E206.MirrorCS", {"start": v(45.95, 3.2) * mm, "end": v(46.05, 3.2) * mm});
            skSolve(sketch);
        }
        {
            var Q0;
            Q0 = qSketchRegion(id + "F18", true);
            extrude(context, id + "F19", {"entities" : qUnion([Q0]), "operationType" : NewBodyOperationType.REMOVE, "oppositeDirection" : true, "depth" : 3 * mm});
        }
        {
            var Q0;
            Q0=qCreatedBy(makeId("Top.planeOp"),FACE);
            var sketch = newSketch(context, id + "F20", { "sketchPlane" : qUnion([Q0])});
            skLineSegment(sketch, "E207", {"start": v(0, 0) * mm, "end": v(-10, 0) * mm, "construction": true});
            skLineSegment(sketch, "E208.bottom", {"start": v(-10, 0) * mm, "end": v(-58, 0) * mm});
            skLineSegment(sketch, "E208.top", {"start": v(-10, 48) * mm, "end": v(-58, 48) * mm});
            skLineSegment(sketch, "E208.left", {"start": v(-10, 0) * mm, "end": v(-10, 48) * mm});
            skLineSegment(sketch, "E208.right", {"start": v(-58, 0) * mm, "end": v(-58, 48) * mm});
            skSolve(sketch);
        }
        {
            var Q0;
            Q0 = qSketchRegion(id + "F20", true);
            extrude(context, id + "F21", {"entities" : qUnion([Q0]), "depth" : 4 * mm});
        }
        {
            var Q0;
            Q0=makeQuery(id+"F21.opExtrude","CAP_FACE",FACE,{"disambiguationData":[OSD([sQuery(id+"F20.wireOp",EDGE,"E208.bottom"),sQuery(id+"F20.wireOp",EDGE,"E208.top"),sQuery(id+"F20.wireOp",EDGE,"E208.left"),sQuery(id+"F20.wireOp",EDGE,"E208.right")])],"isStart":false});
            var sketch = newSketch(context, id + "F22", { "sketchPlane" : qUnion([Q0])});
            skLineSegment(sketch, "E209.bottom", {"start": v(-58, 48) * mm, "end": v(-54, 48) * mm});
            skLineSegment(sketch, "E209.top", {"start": v(-58, 44) * mm, "end": v(-54, 44) * mm});
            skLineSegment(sketch, "E209.left", {"start": v(-58, 48) * mm, "end": v(-58, 44) * mm});
            skLineSegment(sketch, "E209.right", {"start": v(-54, 48) * mm, "end": v(-54, 44) * mm});
            skLineSegment(sketch, "E210.bottom", {"start": v(-10, 48) * mm, "end": v(-14, 48) * mm});
            skLineSegment(sketch, "E210.top", {"start": v(-10, 44) * mm, "end": v(-14, 44) * mm});
            skLineSegment(sketch, "E210.left", {"start": v(-10, 48) * mm, "end": v(-10, 44) * mm});
            skLineSegment(sketch, "E210.right", {"start": v(-14, 48) * mm, "end": v(-14, 44) * mm});
            skLineSegment(sketch, "E211.bottom", {"start": v(-10, 0) * mm, "end": v(-14, 0) * mm});
            skLineSegment(sketch, "E211.top", {"start": v(-10, 4) * mm, "end": v(-14, 4) * mm});
            skLineSegment(sketch, "E211.left", {"start": v(-10, 0) * mm, "end": v(-10, 4) * mm});
            skLineSegment(sketch, "E211.right", {"start": v(-14, 0) * mm, "end": v(-14, 4) * mm});
            skLineSegment(sketch, "E212.bottom", {"start": v(-58, 0) * mm, "end": v(-54, 0) * mm});
            skLineSegment(sketch, "E212.top", {"start": v(-58, 4) * mm, "end": v(-54, 4) * mm});
            skLineSegment(sketch, "E212.left", {"start": v(-58, 0) * mm, "end": v(-58, 4) * mm});
            skLineSegment(sketch, "E212.right", {"start": v(-54, 0) * mm, "end": v(-54, 4) * mm});
            skSolve(sketch);
        }
        {
            var Q0;
            Q0 = qSketchRegion(id + "F22", true);
            extrude(context, id + "F23", {"entities" : qUnion([Q0]), "operationType" : NewBodyOperationType.ADD, "depth" : 2 * mm});
        }
        {
            var Q0;
            Q0=makeQuery(id+"F23.boolean.opBoolean","MERGE",FACE,{"derivedFrom":[makeQuery(id+"F21.opExtrude","SWEPT_FACE",FACE,{"disambiguationData":[OSD([sQuery(id+"F20.wireOp",EDGE,"E208.bottom")])]}),makeQuery(id+"F23.opExtrude","SWEPT_FACE",FACE,{"disambiguationData":[OSD([sQuery(id+"F22.wireOp",EDGE,"E211.bottom")])]}),makeQuery(id+"F23.opExtrude","SWEPT_FACE",FACE,{"disambiguationData":[OSD([sQuery(id+"F22.wireOp",EDGE,"E212.bottom")])]})]});
            var sketch = newSketch(context, id + "F24", { "sketchPlane" : qUnion([Q0])});
            skLineSegment(sketch, "E213", {"start": v(-58, 0) * mm, "end": v(-56, 0) * mm, "construction": true});
            skLineSegment(sketch, "E214", {"start": v(-56, 0) * mm, "end": v(-56, 1) * mm, "construction": true});
            skLineSegment(sketch, "E215", {"start": v(-56, 1) * mm, "end": v(-55.95, 1) * mm});
            skLineSegment(sketch, "E216", {"start": v(-55.25, 1.7) * mm, "end": v(-55.25, 2.5) * mm});
            skLineSegment(sketch, "E217", {"start": v(-55.95, 3.2) * mm, "end": v(-56.05, 3.2) * mm});
            skLineSegment(sketch, "E218", {"start": v(-56.75, 2.5) * mm, "end": v(-56.75, 1.7) * mm});
            skLineSegment(sketch, "E219", {"start": v(-56.05, 1) * mm, "end": v(-56, 1) * mm});
            skPoint(sketch, "E220.visualSharp", {"position": v(-55.25, 3.2) * mm});
            skArc(sketch, "E220.filletArc", {"start": v(-55.25, 2.5) * mm, "mid": v(-55.46, 3) * mm, "end": v(-55.95, 3.2) * mm});
            skPoint(sketch, "E221.visualSharp", {"position": v(-56.75, 3.2) * mm});
            skArc(sketch, "E221.filletArc", {"start": v(-56.05, 3.2) * mm, "mid": v(-56.54, 3) * mm, "end": v(-56.75, 2.5) * mm});
            skPoint(sketch, "E222.visualSharp", {"position": v(-56.75, 1) * mm});
            skArc(sketch, "E222.filletArc", {"start": v(-56.75, 1.7) * mm, "mid": v(-56.54, 1.2) * mm, "end": v(-56.05, 1) * mm});
            skPoint(sketch, "E223.visualSharp", {"position": v(-55.25, 1) * mm});
            skArc(sketch, "E223.filletArc", {"start": v(-55.95, 1) * mm, "mid": v(-55.46, 1.2) * mm, "end": v(-55.25, 1.7) * mm});
            skLineSegment(sketch, "E224", {"start": v(-34, 0) * mm, "end": v(-34, -2) * mm, "construction": true});
            skArc(sketch, "E225.MirrorCS", {"start": v(-11.95, 3.2) * mm, "mid": v(-11.46, 3) * mm, "end": v(-11.25, 2.5) * mm});
            skLineSegment(sketch, "E226.MirrorCS", {"start": v(-11.25, 2.5) * mm, "end": v(-11.25, 1.7) * mm});
            skArc(sketch, "E227.MirrorCS", {"start": v(-11.25, 1.7) * mm, "mid": v(-11.46, 1.2) * mm, "end": v(-11.95, 1) * mm});
            skLineSegment(sketch, "E228.MirrorCS", {"start": v(-11.95, 1) * mm, "end": v(-12, 1) * mm});
            skLineSegment(sketch, "E229.MirrorCS", {"start": v(-12, 1) * mm, "end": v(-12.05, 1) * mm});
            skArc(sketch, "E230.MirrorCS", {"start": v(-12.05, 1) * mm, "mid": v(-12.54, 1.2) * mm, "end": v(-12.75, 1.7) * mm});
            skLineSegment(sketch, "E231.MirrorCS", {"start": v(-12.75, 1.7) * mm, "end": v(-12.75, 2.5) * mm});
            skArc(sketch, "E232.MirrorCS", {"start": v(-12.75, 2.5) * mm, "mid": v(-12.54, 3) * mm, "end": v(-12.05, 3.2) * mm});
            skLineSegment(sketch, "E233.MirrorCS", {"start": v(-12.05, 3.2) * mm, "end": v(-11.95, 3.2) * mm});
            skSolve(sketch);
        }
        {
            var Q0;
            Q0 = qSketchRegion(id + "F24", true);
            extrude(context, id + "F25", {"entities" : qUnion([Q0]), "operationType" : NewBodyOperationType.REMOVE, "oppositeDirection" : true, "depth" : 3 * mm});
        }
        {
            var Q0;
            Q0=makeQuery(id+"F23.boolean.opBoolean","MERGE",FACE,{"derivedFrom":[makeQuery(id+"F21.opExtrude","SWEPT_FACE",FACE,{"disambiguationData":[OSD([sQuery(id+"F20.wireOp",EDGE,"E208.right")])]}),makeQuery(id+"F23.opExtrude","SWEPT_FACE",FACE,{"disambiguationData":[OSD([sQuery(id+"F22.wireOp",EDGE,"E209.left")])]}),makeQuery(id+"F23.opExtrude","SWEPT_FACE",FACE,{"disambiguationData":[OSD([sQuery(id+"F22.wireOp",EDGE,"E212.left")])]})]});
            var sketch = newSketch(context, id + "F26", { "sketchPlane" : qUnion([Q0])});
            skLineSegment(sketch, "E234", {"start": v(0, 0) * mm, "end": v(-2, 0) * mm, "construction": true});
            skLineSegment(sketch, "E235", {"start": v(-2, 0) * mm, "end": v(-2, 1) * mm, "construction": true});
            skLineSegment(sketch, "E236", {"start": v(-2, 1) * mm, "end": v(-1.95, 1) * mm});
            skLineSegment(sketch, "E237", {"start": v(-1.25, 1.7) * mm, "end": v(-1.25, 2.5) * mm});
            skLineSegment(sketch, "E238", {"start": v(-1.95, 3.2) * mm, "end": v(-2.05, 3.2) * mm});
            skLineSegment(sketch, "E239", {"start": v(-2.75, 2.5) * mm, "end": v(-2.75, 1.7) * mm});
            skLineSegment(sketch, "E240", {"start": v(-2.05, 1) * mm, "end": v(-2, 1) * mm});
            skPoint(sketch, "E241.visualSharp", {"position": v(-2.75, 3.2) * mm});
            skArc(sketch, "E241.filletArc", {"start": v(-2.05, 3.2) * mm, "mid": v(-2.54, 3) * mm, "end": v(-2.75, 2.5) * mm});
            skPoint(sketch, "E242.visualSharp", {"position": v(-2.75, 1) * mm});
            skArc(sketch, "E242.filletArc", {"start": v(-2.75, 1.7) * mm, "mid": v(-2.54, 1.2) * mm, "end": v(-2.05, 1) * mm});
            skPoint(sketch, "E243.visualSharp", {"position": v(-1.25, 1) * mm});
            skArc(sketch, "E243.filletArc", {"start": v(-1.95, 1) * mm, "mid": v(-1.46, 1.2) * mm, "end": v(-1.25, 1.7) * mm});
            skPoint(sketch, "E244.visualSharp", {"position": v(-1.25, 3.2) * mm});
            skArc(sketch, "E244.filletArc", {"start": v(-1.25, 2.5) * mm, "mid": v(-1.46, 3) * mm, "end": v(-1.95, 3.2) * mm});
            skLineSegment(sketch, "E245", {"start": v(-24, 0) * mm, "end": v(-24, -4.44) * mm});
            skArc(sketch, "E246.MirrorCS", {"start": v(-45.95, 3.2) * mm, "mid": v(-45.46, 3) * mm, "end": v(-45.25, 2.5) * mm});
            skLineSegment(sketch, "E247.MirrorCS", {"start": v(-45.25, 2.5) * mm, "end": v(-45.25, 1.7) * mm});
            skArc(sketch, "E248.MirrorCS", {"start": v(-45.25, 1.7) * mm, "mid": v(-45.46, 1.2) * mm, "end": v(-45.95, 1) * mm});
            skLineSegment(sketch, "E249.MirrorCS", {"start": v(-45.95, 1) * mm, "end": v(-46, 1) * mm});
            skLineSegment(sketch, "E250.MirrorCS", {"start": v(-46, 1) * mm, "end": v(-46.05, 1) * mm});
            skArc(sketch, "E251.MirrorCS", {"start": v(-46.05, 1) * mm, "mid": v(-46.54, 1.2) * mm, "end": v(-46.75, 1.7) * mm});
            skLineSegment(sketch, "E252.MirrorCS", {"start": v(-46.75, 1.7) * mm, "end": v(-46.75, 2.5) * mm});
            skArc(sketch, "E253.MirrorCS", {"start": v(-46.75, 2.5) * mm, "mid": v(-46.54, 3) * mm, "end": v(-46.05, 3.2) * mm});
            skLineSegment(sketch, "E254.MirrorCS", {"start": v(-46.05, 3.2) * mm, "end": v(-45.95, 3.2) * mm});
            skSolve(sketch);
        }
        {
            var Q0;
            Q0 = qSketchRegion(id + "F26", true);
            extrude(context, id + "F27", {"entities" : qUnion([Q0]), "operationType" : NewBodyOperationType.REMOVE, "oppositeDirection" : true, "depth" : 3 * mm});
        }
        {
            var Q0;
            Q0=makeQuery(id+"F23.boolean.opBoolean","MERGE",FACE,{"derivedFrom":[makeQuery(id+"F21.opExtrude","SWEPT_FACE",FACE,{"disambiguationData":[OSD([sQuery(id+"F20.wireOp",EDGE,"E208.top")])]}),makeQuery(id+"F23.opExtrude","SWEPT_FACE",FACE,{"disambiguationData":[OSD([sQuery(id+"F22.wireOp",EDGE,"E209.bottom")])]}),makeQuery(id+"F23.opExtrude","SWEPT_FACE",FACE,{"disambiguationData":[OSD([sQuery(id+"F22.wireOp",EDGE,"E210.bottom")])]})]});
            var sketch = newSketch(context, id + "F28", { "sketchPlane" : qUnion([Q0])});
            skLineSegment(sketch, "E255", {"start": v(58, 0) * mm, "end": v(56, 0) * mm, "construction": true});
            skLineSegment(sketch, "E256", {"start": v(56, 0) * mm, "end": v(56, 1) * mm, "construction": true});
            skLineSegment(sketch, "E257", {"start": v(56, 1) * mm, "end": v(56.05, 1) * mm});
            skLineSegment(sketch, "E258", {"start": v(56.75, 1.7) * mm, "end": v(56.75, 2.5) * mm});
            skLineSegment(sketch, "E259", {"start": v(56.05, 3.2) * mm, "end": v(55.95, 3.2) * mm});
            skLineSegment(sketch, "E260", {"start": v(55.25, 2.5) * mm, "end": v(55.25, 1.7) * mm});
            skLineSegment(sketch, "E261", {"start": v(55.95, 1) * mm, "end": v(56, 1) * mm});
            skPoint(sketch, "E262.visualSharp", {"position": v(56.75, 3.2) * mm});
            skArc(sketch, "E262.filletArc", {"start": v(56.75, 2.5) * mm, "mid": v(56.54, 3) * mm, "end": v(56.05, 3.2) * mm});
            skPoint(sketch, "E263.visualSharp", {"position": v(55.25, 3.2) * mm});
            skArc(sketch, "E263.filletArc", {"start": v(55.95, 3.2) * mm, "mid": v(55.46, 3) * mm, "end": v(55.25, 2.5) * mm});
            skPoint(sketch, "E264.visualSharp", {"position": v(55.25, 1) * mm});
            skArc(sketch, "E264.filletArc", {"start": v(55.25, 1.7) * mm, "mid": v(55.46, 1.2) * mm, "end": v(55.95, 1) * mm});
            skPoint(sketch, "E265.visualSharp", {"position": v(56.75, 1) * mm});
            skArc(sketch, "E265.filletArc", {"start": v(56.05, 1) * mm, "mid": v(56.54, 1.2) * mm, "end": v(56.75, 1.7) * mm});
            skLineSegment(sketch, "E266", {"start": v(34, 0) * mm, "end": v(34, -2.92) * mm, "construction": true});
            skLineSegment(sketch, "E267.MirrorCS", {"start": v(11.95, 3.2) * mm, "end": v(12.05, 3.2) * mm});
            skArc(sketch, "E268.MirrorCS", {"start": v(12.05, 3.2) * mm, "mid": v(12.54, 3) * mm, "end": v(12.75, 2.5) * mm});
            skLineSegment(sketch, "E269.MirrorCS", {"start": v(12.75, 2.5) * mm, "end": v(12.75, 1.7) * mm});
            skArc(sketch, "E270.MirrorCS", {"start": v(12.75, 1.7) * mm, "mid": v(12.54, 1.2) * mm, "end": v(12.05, 1) * mm});
            skLineSegment(sketch, "E271.MirrorCS", {"start": v(12.05, 1) * mm, "end": v(12, 1) * mm});
            skLineSegment(sketch, "E272.MirrorCS", {"start": v(12, 1) * mm, "end": v(11.95, 1) * mm});
            skArc(sketch, "E273.MirrorCS", {"start": v(11.95, 1) * mm, "mid": v(11.46, 1.2) * mm, "end": v(11.25, 1.7) * mm});
            skLineSegment(sketch, "E274.MirrorCS", {"start": v(11.25, 1.7) * mm, "end": v(11.25, 2.5) * mm});
            skArc(sketch, "E275.MirrorCS", {"start": v(11.25, 2.5) * mm, "mid": v(11.46, 3) * mm, "end": v(11.95, 3.2) * mm});
            skSolve(sketch);
        }
        {
            var Q0;
            Q0 = qSketchRegion(id + "F28", true);
            extrude(context, id + "F29", {"entities" : qUnion([Q0]), "operationType" : NewBodyOperationType.REMOVE, "oppositeDirection" : true, "depth" : 3 * mm});
        }
        {
            var Q0;
            Q0=makeQuery(id+"F23.boolean.opBoolean","MERGE",FACE,{"derivedFrom":[makeQuery(id+"F21.opExtrude","SWEPT_FACE",FACE,{"disambiguationData":[OSD([sQuery(id+"F20.wireOp",EDGE,"E208.left")])]}),makeQuery(id+"F23.opExtrude","SWEPT_FACE",FACE,{"disambiguationData":[OSD([sQuery(id+"F22.wireOp",EDGE,"E210.left")])]}),makeQuery(id+"F23.opExtrude","SWEPT_FACE",FACE,{"disambiguationData":[OSD([sQuery(id+"F22.wireOp",EDGE,"E211.left")])]})]});
            var sketch = newSketch(context, id + "F30", { "sketchPlane" : qUnion([Q0])});
            skLineSegment(sketch, "E276", {"start": v(48, 0) * mm, "end": v(46, 0) * mm, "construction": true});
            skLineSegment(sketch, "E277", {"start": v(46, 0) * mm, "end": v(46, 1) * mm, "construction": true});
            skLineSegment(sketch, "E278", {"start": v(46, 1) * mm, "end": v(46.05, 1) * mm});
            skLineSegment(sketch, "E279", {"start": v(46.75, 1.7) * mm, "end": v(46.75, 2.5) * mm});
            skLineSegment(sketch, "E280", {"start": v(46.05, 3.2) * mm, "end": v(45.95, 3.2) * mm});
            skLineSegment(sketch, "E281", {"start": v(45.25, 2.5) * mm, "end": v(45.25, 1.7) * mm});
            skLineSegment(sketch, "E282", {"start": v(45.95, 1) * mm, "end": v(46, 1) * mm});
            skPoint(sketch, "E283.visualSharp", {"position": v(46.75, 3.2) * mm});
            skArc(sketch, "E283.filletArc", {"start": v(46.75, 2.5) * mm, "mid": v(46.54, 3) * mm, "end": v(46.05, 3.2) * mm});
            skPoint(sketch, "E284.visualSharp", {"position": v(45.25, 3.2) * mm});
            skArc(sketch, "E284.filletArc", {"start": v(45.95, 3.2) * mm, "mid": v(45.46, 3) * mm, "end": v(45.25, 2.5) * mm});
            skPoint(sketch, "E285.visualSharp", {"position": v(45.25, 1) * mm});
            skArc(sketch, "E285.filletArc", {"start": v(45.25, 1.7) * mm, "mid": v(45.46, 1.2) * mm, "end": v(45.95, 1) * mm});
            skPoint(sketch, "E286.visualSharp", {"position": v(46.75, 1) * mm});
            skArc(sketch, "E286.filletArc", {"start": v(46.05, 1) * mm, "mid": v(46.54, 1.2) * mm, "end": v(46.75, 1.7) * mm});
            skLineSegment(sketch, "E287", {"start": v(24, 0) * mm, "end": v(24, -2.8) * mm, "construction": true});
            skArc(sketch, "E288.MirrorCS", {"start": v(2.05, 3.2) * mm, "mid": v(2.54, 3) * mm, "end": v(2.75, 2.5) * mm});
            skLineSegment(sketch, "E289.MirrorCS", {"start": v(2.75, 2.5) * mm, "end": v(2.75, 1.7) * mm});
            skArc(sketch, "E290.MirrorCS", {"start": v(2.75, 1.7) * mm, "mid": v(2.54, 1.2) * mm, "end": v(2.05, 1) * mm});
            skLineSegment(sketch, "E291.MirrorCS", {"start": v(2.05, 1) * mm, "end": v(2, 1) * mm});
            skLineSegment(sketch, "E292.MirrorCS", {"start": v(2, 1) * mm, "end": v(1.95, 1) * mm});
            skArc(sketch, "E293.MirrorCS", {"start": v(1.95, 1) * mm, "mid": v(1.46, 1.2) * mm, "end": v(1.25, 1.7) * mm});
            skLineSegment(sketch, "E294.MirrorCS", {"start": v(1.25, 1.7) * mm, "end": v(1.25, 2.5) * mm});
            skArc(sketch, "E295.MirrorCS", {"start": v(1.25, 2.5) * mm, "mid": v(1.46, 3) * mm, "end": v(1.95, 3.2) * mm});
            skLineSegment(sketch, "E296.MirrorCS", {"start": v(1.95, 3.2) * mm, "end": v(2.05, 3.2) * mm});
            skSolve(sketch);
        }
        {
            var Q0;
            Q0 = qSketchRegion(id + "F30", true);
            extrude(context, id + "F31", {"entities" : qUnion([Q0]), "operationType" : NewBodyOperationType.REMOVE, "oppositeDirection" : true, "depth" : 3 * mm});
        }
        {
            var Q0;
            Q0=makeQuery(id+"F21.opExtrude","CAP_FACE",FACE,{"disambiguationData":[OSD([sQuery(id+"F20.wireOp",EDGE,"E208.bottom"),sQuery(id+"F20.wireOp",EDGE,"E208.top"),sQuery(id+"F20.wireOp",EDGE,"E208.left"),sQuery(id+"F20.wireOp",EDGE,"E208.right")])],"isStart":true});
            var sketch = newSketch(context, id + "F32", { "sketchPlane" : qUnion([Q0])});
            skLineSegment(sketch, "E297", {"start": v(-58, 0) * mm, "end": v(-56, 0) * mm, "construction": true});
            skLineSegment(sketch, "E298", {"start": v(-56, 0) * mm, "end": v(-56, -2) * mm, "construction": true});
            skCircle(sketch, "E299", {"center": v(-56, -2) * mm, "radius": 0.75 * mm});
            skLineSegment(sketch, "E300", {"start": v(-34, 0) * mm, "end": v(-34, -4.4) * mm, "construction": true});
            skPoint(sketch, "E300.endSnap0", {"position": v(-34, 0) * mm});
            skCircle(sketch, "E301.MirrorC", {"center": v(-12, -2) * mm, "radius": 0.75 * mm});
            skLineSegment(sketch, "E302", {"start": v(-58, -24) * mm, "end": v(-65.93, -24) * mm, "construction": true});
            skCircle(sketch, "E303.MirrorC", {"center": v(-56, -46) * mm, "radius": 0.75 * mm});
            skCircle(sketch, "E304.MirrorC", {"center": v(-12, -46) * mm, "radius": 0.75 * mm});
            skSolve(sketch);
        }
        {
            var Q0;
            Q0 = qSketchRegion(id + "F32", true);
            extrude(context, id + "F33", {"entities" : qUnion([Q0]), "operationType" : NewBodyOperationType.REMOVE, "oppositeDirection" : true, "depth" : 2.5 * mm});
        }
    });
